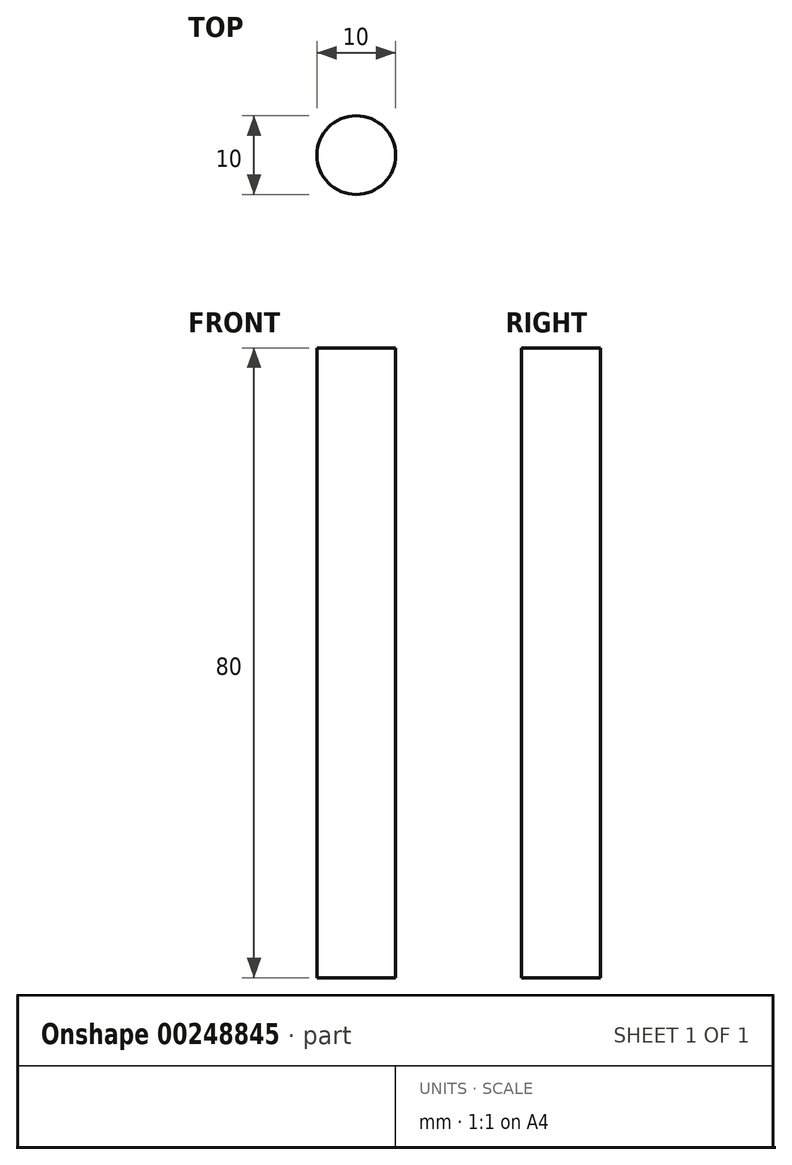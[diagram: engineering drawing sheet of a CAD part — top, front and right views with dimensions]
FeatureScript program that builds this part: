
annotation { "Feature Type Name" : "Feature", "Feature Type Description" : "" }
export const myFeature = defineFeature(function(context is Context, id is Id, definition is map)
    precondition{}
    {
        {
            var Q0;
            Q0=qCreatedBy(makeId("Top.planeOp"),FACE);
            var sketch = newSketch(context, id + "F0", { "sketchPlane" : qUnion([Q0])});
            skCircle(sketch, "E0", {"center": v(0, 0) * mm, "radius": 5 * mm});
            skSolve(sketch);
        }
        {
            var Q0;
            Q0=makeQuery(id+"F0.imprint","IMPRINT",FACE,{"disambiguationData":[TD([[makeQuery(id+"F0.imprint","IMPRINT",EDGE,{"derivedFrom":sQuery(id+"F0.wireOp",EDGE,"E0")}),1.0]])]});
            extrude(context, id + "F1", {"entities" : qUnion([Q0]), "endBound" : BoundingType.SYMMETRIC, "depth" : 80 * mm});
        }
    });
